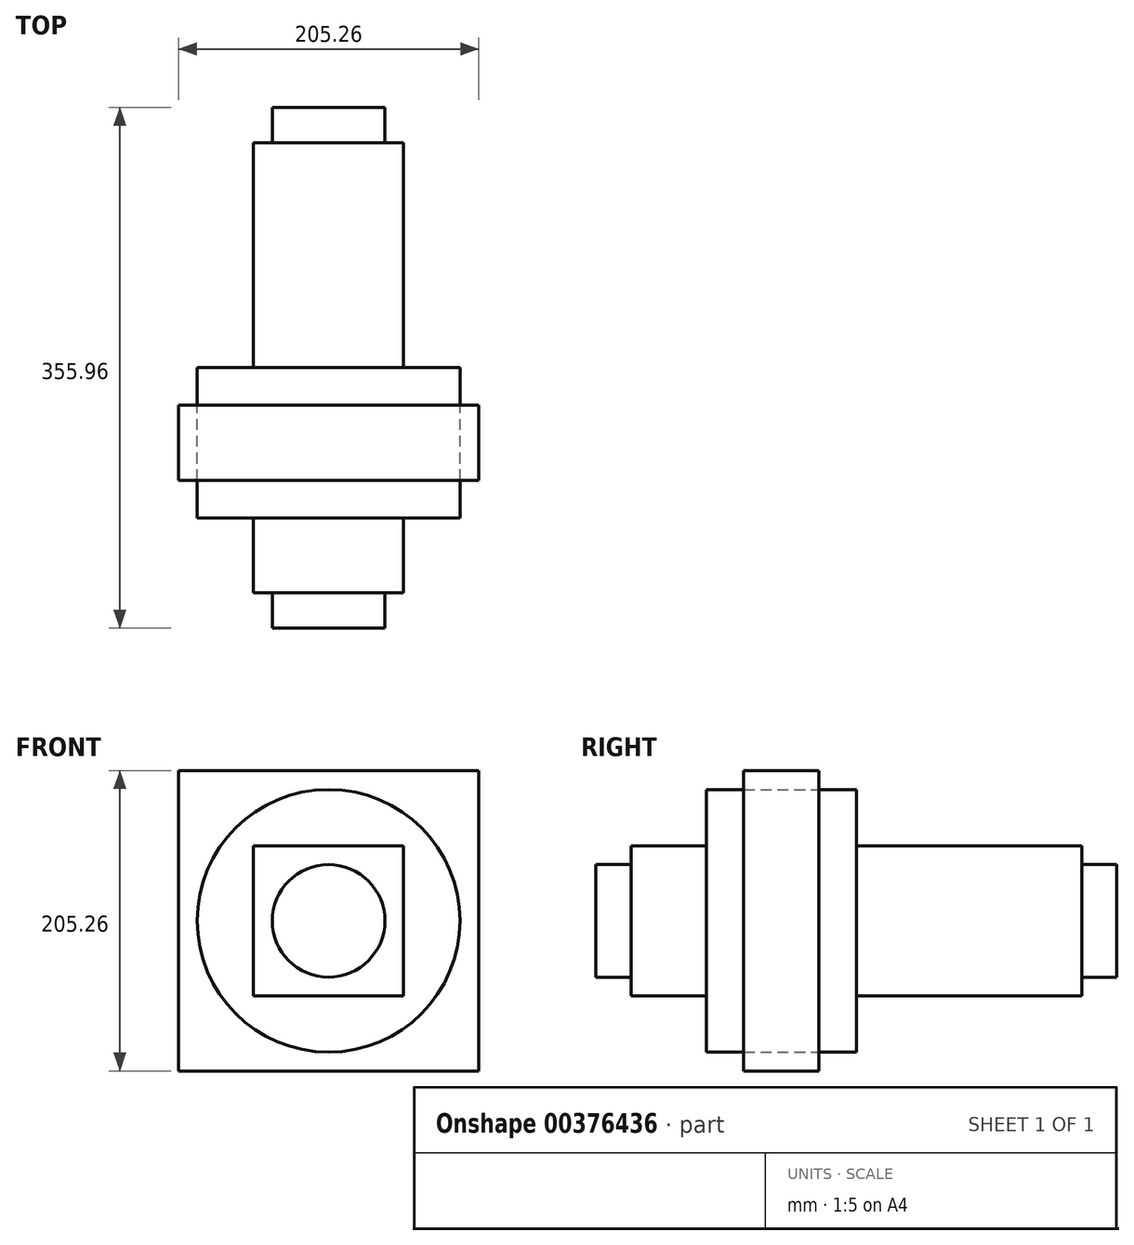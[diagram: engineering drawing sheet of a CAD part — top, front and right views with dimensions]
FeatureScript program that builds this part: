
annotation { "Feature Type Name" : "Feature", "Feature Type Description" : "" }
export const myFeature = defineFeature(function(context is Context, id is Id, definition is map)
    precondition{}
    {
        {
            var Q0;
            Q0=qCreatedBy(makeId("Front.planeOp"),FACE);
            var sketch = newSketch(context, id + "F0", { "sketchPlane" : qUnion([Q0])});
            skLineSegment(sketch, "E0.bottom", {"start": v(102.63, -102.63) * mm, "end": v(-102.63, -102.63) * mm});
            skLineSegment(sketch, "E0.top", {"start": v(102.63, 102.63) * mm, "end": v(-102.63, 102.63) * mm});
            skLineSegment(sketch, "E0.left", {"start": v(102.63, -102.63) * mm, "end": v(102.63, 102.63) * mm});
            skLineSegment(sketch, "E0.right", {"start": v(-102.63, -102.63) * mm, "end": v(-102.63, 102.63) * mm});
            skPoint(sketch, "E0.middle", {"position": v(0, 0) * mm});
            skCircle(sketch, "E1", {"center": v(0, 0) * mm, "radius": 89.8 * mm});
            skSolve(sketch);
        }
        {
            var Q0;
            Q0=qSketchRegion(id+"F0",true);
            extrude(context, id + "F1", {"entities" : qUnion([Q0]), "depth" : 51.31 * mm, "symmetric" : true});
        }
        {
            var Q0;
            Q0=makeQuery(id+"F0.imprint","IMPRINT",FACE,{"disambiguationData":[TD([[makeQuery(id+"F0.imprint","IMPRINT",EDGE,{"derivedFrom":sQuery(id+"F0.wireOp",EDGE,"E1")}),1.0]])]});
            extrude(context, id + "F2", {"entities" : qUnion([Q0]), "depth" : 102.62 * mm, "symmetric" : true});
        }
        {
            var Q0;
            Q0=makeQuery(id+"F2.opExtrude","CAP_FACE",FACE,{"disambiguationData":[OSD([sQuery(id+"F0.wireOp",EDGE,"E1")])],"isStart":true});
            var sketch = newSketch(context, id + "F3", { "sketchPlane" : qUnion([Q0])});
            skLineSegment(sketch, "E2.bottom", {"start": v(51.3, -51.3) * mm, "end": v(-51.3, -51.3) * mm});
            skLineSegment(sketch, "E2.top", {"start": v(51.3, 51.3) * mm, "end": v(-51.3, 51.3) * mm});
            skLineSegment(sketch, "E2.left", {"start": v(51.3, -51.3) * mm, "end": v(51.3, 51.3) * mm});
            skLineSegment(sketch, "E2.right", {"start": v(-51.3, -51.3) * mm, "end": v(-51.3, 51.3) * mm});
            skPoint(sketch, "E2.middle", {"position": v(0, 0) * mm});
            skCircle(sketch, "E3", {"center": v(0, 0) * mm, "radius": 38.5 * mm});
            skSolve(sketch);
        }
        {
            var Q0;
            Q0=makeQuery(id+"F3.imprint","IMPRINT",FACE,{"disambiguationData":[TD([[makeQuery(id+"F3.imprint","IMPRINT",EDGE,{"derivedFrom":sQuery(id+"F3.wireOp",EDGE,"E2.bottom")}),-1.0]])]});
            extrude(context, id + "F4", {"entities" : qUnion([Q0]), "operationType" : NewBodyOperationType.ADD, "depth" : 307.85 * mm, "symmetric" : true});
        }
        {
            var Q0;
            Q0=makeQuery(id+"F4.boolean.opBoolean","SPLIT",FACE,{"disambiguationData":[TD([makeQuery(id+"F4.opExtrude","SWEPT_FACE",FACE,{"disambiguationData":[OSD([sQuery(id+"F3.wireOp",EDGE,"E3")])]})])],"derivedFrom":makeQuery(id+"F2.opExtrude","CAP_FACE",FACE,{"disambiguationData":[OSD([sQuery(id+"F0.wireOp",EDGE,"E1")])],"isStart":true})});
            extrude(context, id + "F5", {"entities" : qUnion([Q0]), "operationType" : NewBodyOperationType.ADD, "depth" : 355.96 * mm, "symmetric" : true});
        }
    });
